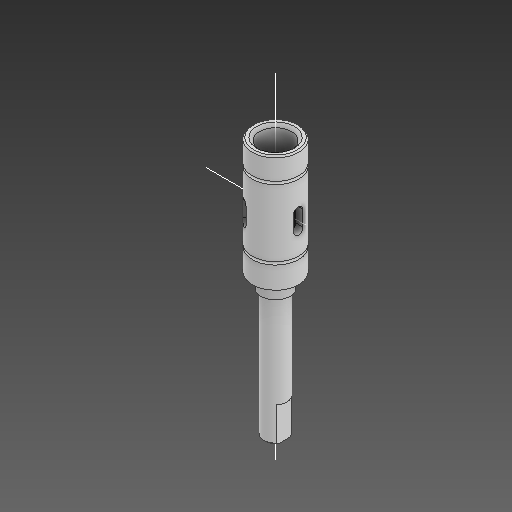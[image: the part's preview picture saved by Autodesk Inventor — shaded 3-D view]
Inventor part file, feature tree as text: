
AUTODESK INVENTOR PART (.ipt)
format: ipt  version: 2021 (Build 250183000, 183)  size: 228,352 bytes
history: native  units: in
note: dims shown in document units (in); Inventor stores cm internally (conversion verified against a paired STEP export)
features: sketch x10, other x8, plane x3
ambient origin geometry x8: Origin, YZ Plane, XZ Plane, XY Plane, X Axis, Y Axis, Z Axis, Center Point
bodies: Solid1 (feature_tree)
feature tree (21):
  other  "iner_sleeve.ipt"
  other  "Solid1::iner_sleeve.ipt"
  other  "TaggingFeature1"
  sketch  "Sketch1"  dims[d0=0.3937in]
  sketch  "Sketch2"
  sketch  "Sketch3"
  sketch  "Sketch5"
  sketch  "Sketch6"
  sketch  "Sketch7"
  sketch  "Sketch8"
  sketch  "Sketch10"
  sketch  "Sketch11"
  sketch  "Sketch12"
  plane  "Work Plane1"
  plane  "Work Plane2"
  plane  "Work Plane3"
  other  "Work Axis1"
  other  "Work Axis2"
  other  "Work Axis3"
  other  "Srf1"
  other  "Srf1::Derived"
